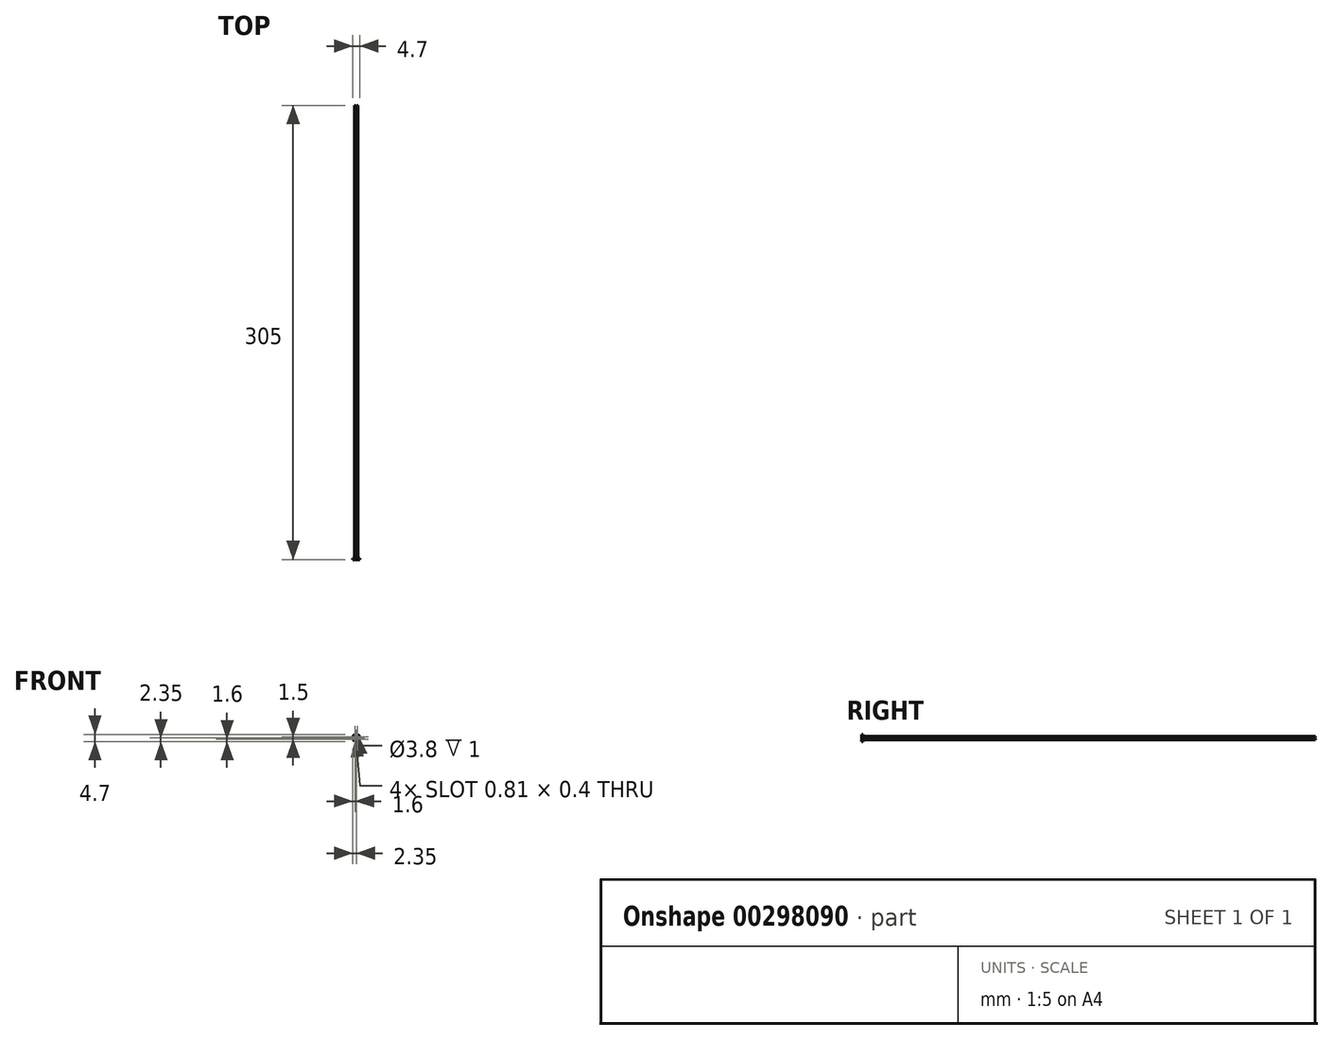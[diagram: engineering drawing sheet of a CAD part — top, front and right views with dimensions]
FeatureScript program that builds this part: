
annotation { "Feature Type Name" : "Feature", "Feature Type Description" : "" }
export const myFeature = defineFeature(function(context is Context, id is Id, definition is map)
    precondition{}
    {
        {
            var Q0;
            Q0=qCreatedBy(makeId("Front.planeOp"),FACE);
            var sketch = newSketch(context, id + "F0", { "sketchPlane" : qUnion([Q0])});
            skCircle(sketch, "E0", {"center": v(0, 0) * mm, "radius": 2.35 * mm});
            skPoint(sketch, "E1", {"position": v(0.75, 0.55) * mm});
            skCircle(sketch, "E2", {"center": v(0.75, 0.55) * mm, "radius": 0.2 * mm});
            skCircle(sketch, "E3", {"center": v(0.75, 0.95) * mm, "radius": 0.2 * mm});
            skCircle(sketch, "E4", {"center": v(0.75, 0.75) * mm, "radius": 0.44 * mm});
            skCircle(sketch, "E5", {"center": v(0, 0) * mm, "radius": 1.91 * mm});
            skCircle(sketch, "E6.1.0", {"center": v(-0.75, 0.75) * mm, "radius": 0.44 * mm});
            skCircle(sketch, "E6.1.1", {"center": v(-0.95, 0.75) * mm, "radius": 0.2 * mm});
            skCircle(sketch, "E6.1.2", {"center": v(-0.55, 0.75) * mm, "radius": 0.2 * mm});
            skCircle(sketch, "E6.2.0", {"center": v(-0.75, -0.75) * mm, "radius": 0.44 * mm});
            skCircle(sketch, "E6.2.1", {"center": v(-0.75, -0.95) * mm, "radius": 0.2 * mm});
            skCircle(sketch, "E6.2.2", {"center": v(-0.75, -0.55) * mm, "radius": 0.2 * mm});
            skCircle(sketch, "E6.3.0", {"center": v(0.75, -0.75) * mm, "radius": 0.44 * mm});
            skCircle(sketch, "E6.3.1", {"center": v(0.95, -0.75) * mm, "radius": 0.2 * mm});
            skCircle(sketch, "E6.3.2", {"center": v(0.55, -0.75) * mm, "radius": 0.2 * mm});
            skSolve(sketch);
        }
        {
            var Q0;
            Q0=makeQuery(id+"F0.imprint","IMPRINT",FACE,{"disambiguationData":[TD([[makeQuery(id+"F0.imprint","IMPRINT",EDGE,{"derivedFrom":sQuery(id+"F0.wireOp",EDGE,"E6.1.1")}),1.0]])]});
            var Q1;
            Q1=makeQuery(id+"F0.imprint","IMPRINT",FACE,{"disambiguationData":[TD([[makeQuery(id+"F0.imprint","IMPRINT",EDGE,{"derivedFrom":sQuery(id+"F0.wireOp",EDGE,"E6.1.2")}),1.0]])]});
            var Q2;
            Q2=makeQuery(id+"F0.imprint","IMPRINT",FACE,{"disambiguationData":[TD([[makeQuery(id+"F0.imprint","IMPRINT",EDGE,{"derivedFrom":sQuery(id+"F0.wireOp",EDGE,"E3")}),1.0]])]});
            var Q3;
            Q3=makeQuery(id+"F0.imprint","IMPRINT",FACE,{"disambiguationData":[TD([[makeQuery(id+"F0.imprint","IMPRINT",EDGE,{"derivedFrom":sQuery(id+"F0.wireOp",EDGE,"E2")}),1.0]])]});
            var Q4;
            Q4=makeQuery(id+"F0.imprint","IMPRINT",FACE,{"disambiguationData":[TD([[makeQuery(id+"F0.imprint","IMPRINT",EDGE,{"derivedFrom":sQuery(id+"F0.wireOp",EDGE,"E6.2.2")}),1.0]])]});
            var Q5;
            Q5=makeQuery(id+"F0.imprint","IMPRINT",FACE,{"disambiguationData":[TD([[makeQuery(id+"F0.imprint","IMPRINT",EDGE,{"derivedFrom":sQuery(id+"F0.wireOp",EDGE,"E6.2.1")}),1.0]])]});
            var Q6;
            Q6=makeQuery(id+"F0.imprint","IMPRINT",FACE,{"disambiguationData":[TD([[makeQuery(id+"F0.imprint","IMPRINT",EDGE,{"derivedFrom":sQuery(id+"F0.wireOp",EDGE,"E6.3.2")}),1.0]])]});
            var Q7;
            Q7=makeQuery(id+"F0.imprint","IMPRINT",FACE,{"disambiguationData":[TD([[makeQuery(id+"F0.imprint","IMPRINT",EDGE,{"derivedFrom":sQuery(id+"F0.wireOp",EDGE,"E6.3.1")}),1.0]])]});
            extrude(context, id + "F1", {"entities" : qUnion([Q0, Q1, Q2, Q3, Q4, Q5, Q6, Q7]), "depth" : 305 * mm});
        }
        {
            var Q0;
            Q0=makeQuery(id+"F1.opExtrude","CAP_FACE",FACE,{"disambiguationData":[OSD([sQuery(id+"F0.wireOp",EDGE,"E3")])],"isStart":false});
            var sketch = newSketch(context, id + "F2", { "sketchPlane" : qUnion([Q0])});
            skCircle(sketch, "E7.0.0", {"center": v(0.75, 0.95) * mm, "radius": 0.2 * mm});
            skCircle(sketch, "E8.0.0", {"center": v(0.75, 0.55) * mm, "radius": 0.2 * mm});
            skCircle(sketch, "E9.0.0", {"center": v(-0.55, 0.75) * mm, "radius": 0.2 * mm});
            skCircle(sketch, "E10.0.0", {"center": v(-0.95, 0.75) * mm, "radius": 0.2 * mm});
            skCircle(sketch, "E11.0.0", {"center": v(-0.75, -0.55) * mm, "radius": 0.2 * mm});
            skCircle(sketch, "E12.0.0", {"center": v(-0.75, -0.95) * mm, "radius": 0.2 * mm});
            skCircle(sketch, "E13.0.0", {"center": v(0.55, -0.75) * mm, "radius": 0.2 * mm});
            skCircle(sketch, "E14.0.0", {"center": v(0.95, -0.75) * mm, "radius": 0.2 * mm});
            skCircle(sketch, "E15", {"center": v(0.75, 0.75) * mm, "radius": 0.44 * mm});
            skLineSegment(sketch, "E16", {"start": v(0.55, 0.95) * mm, "end": v(0.55, 0.55) * mm});
            skLineSegment(sketch, "E17", {"start": v(0.95, 0.95) * mm, "end": v(0.95, 0.55) * mm});
            skCircle(sketch, "E18.1.0", {"center": v(-0.75, 0.75) * mm, "radius": 0.44 * mm});
            skLineSegment(sketch, "E18.1.1", {"start": v(-0.95, 0.95) * mm, "end": v(-0.55, 0.95) * mm});
            skCircle(sketch, "E18.2.0", {"center": v(-0.75, -0.75) * mm, "radius": 0.44 * mm});
            skLineSegment(sketch, "E18.2.1", {"start": v(-0.95, -0.95) * mm, "end": v(-0.95, -0.55) * mm});
            skCircle(sketch, "E18.3.0", {"center": v(0.75, -0.75) * mm, "radius": 0.44 * mm});
            skLineSegment(sketch, "E18.3.1", {"start": v(0.95, -0.95) * mm, "end": v(0.55, -0.95) * mm});
            skPoint(sketch, "E18.center", {"position": v(0, 0) * mm});
            skLineSegment(sketch, "E19", {"start": v(-0.95, 0.55) * mm, "end": v(-0.55, 0.55) * mm});
            skLineSegment(sketch, "E20", {"start": v(-0.55, -0.55) * mm, "end": v(-0.55, -0.95) * mm});
            skLineSegment(sketch, "E21", {"start": v(0.55, -0.55) * mm, "end": v(0.95, -0.55) * mm});
            skSolve(sketch);
        }
        {
            var Q0;
            Q0=makeQuery(id+"F2.imprint","IMPRINT",FACE,{"disambiguationData":[TD([[makeQuery(id+"F2.imprint","IMPRINT",EDGE,{"derivedFrom":sQuery(id+"F2.wireOp",EDGE,"E15")}),1.0]])]});
            var Q1;
            Q1=makeQuery(id+"F2.imprint","IMPRINT",FACE,{"disambiguationData":[TD([[makeQuery(id+"F2.imprint","IMPRINT",EDGE,{"derivedFrom":sQuery(id+"F2.wireOp",EDGE,"E18.1.0")}),1.0]])]});
            var Q2;
            Q2=makeQuery(id+"F2.imprint","IMPRINT",FACE,{"disambiguationData":[TD([[makeQuery(id+"F2.imprint","IMPRINT",EDGE,{"derivedFrom":sQuery(id+"F2.wireOp",EDGE,"E18.2.0")}),1.0]])]});
            var Q3;
            Q3=makeQuery(id+"F2.imprint","IMPRINT",FACE,{"disambiguationData":[TD([[makeQuery(id+"F2.imprint","IMPRINT",EDGE,{"derivedFrom":sQuery(id+"F2.wireOp",EDGE,"E18.3.0")}),1.0]])]});
            extrude(context, id + "F3", {"entities" : qUnion([Q0, Q1, Q2, Q3]), "oppositeDirection" : true, "depth" : 1 * mm});
        }
        {
            var Q0;
            Q0=makeQuery(id+"F3.opExtrude","CAP_FACE",FACE,{"disambiguationData":[OSD([sQuery(id+"F2.wireOp",EDGE,"E9.0.0"),sQuery(id+"F2.wireOp",EDGE,"E10.0.0"),sQuery(id+"F2.wireOp",EDGE,"E18.1.0"),sQuery(id+"F2.wireOp",EDGE,"E18.1.1"),sQuery(id+"F2.wireOp",EDGE,"E19")])],"isStart":true});
            var sketch = newSketch(context, id + "F4", { "sketchPlane" : qUnion([Q0])});
            skCircle(sketch, "E22", {"center": v(0, 0) * mm, "radius": 1.9 * mm});
            skCircle(sketch, "E23", {"center": v(0, 0) * mm, "radius": 2.35 * mm});
            skSolve(sketch);
        }
        {
            var Q0;
            Q0=makeQuery(id+"F4.imprint","IMPRINT",FACE,{"disambiguationData":[TD([[makeQuery(id+"F4.imprint","IMPRINT",EDGE,{"derivedFrom":sQuery(id+"F4.wireOp",EDGE,"E22")}),-1.0]])]});
            extrude(context, id + "F5", {"entities" : qUnion([Q0]), "oppositeDirection" : true, "depth" : 1 * mm});
        }
    });
